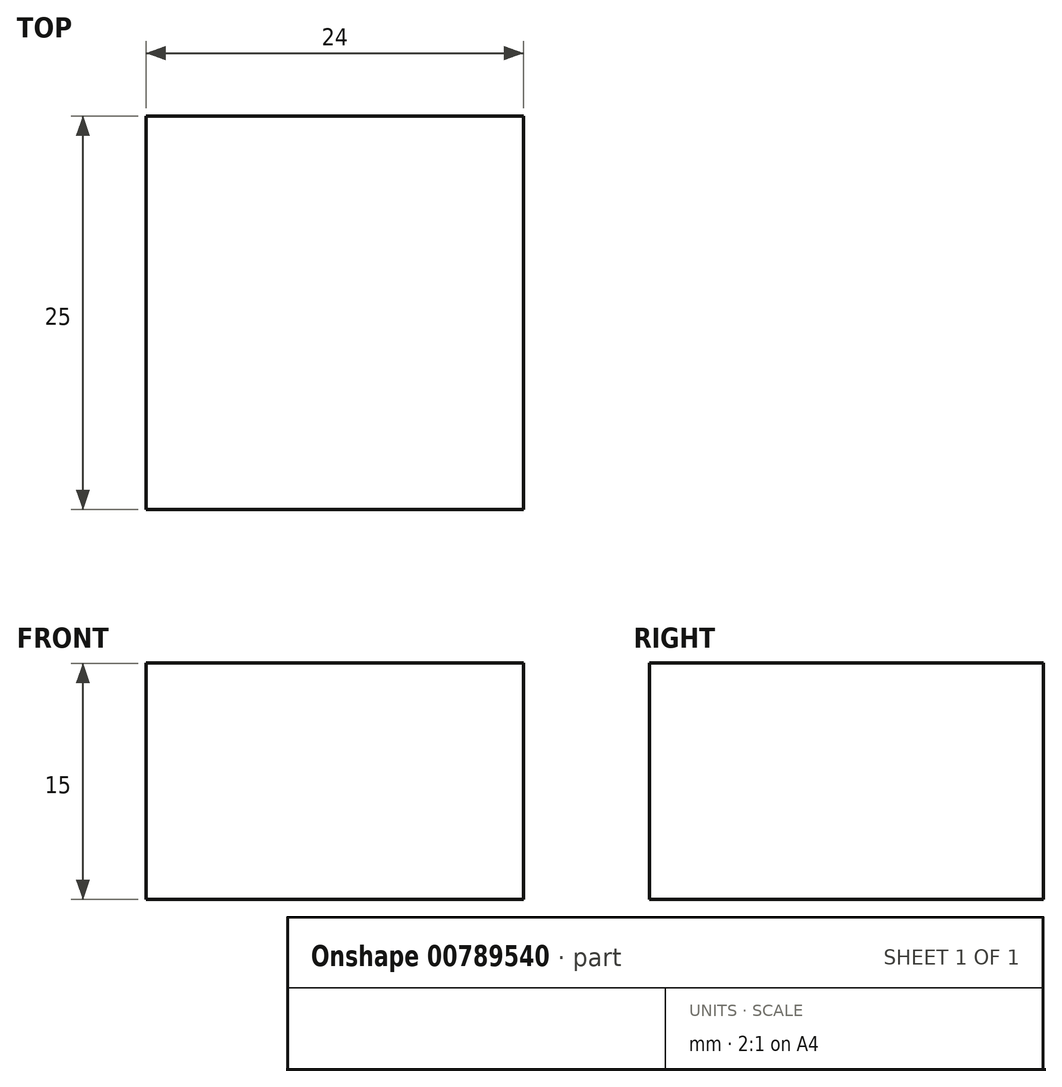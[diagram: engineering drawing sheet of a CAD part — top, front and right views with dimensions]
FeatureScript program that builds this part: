
annotation { "Feature Type Name" : "Feature", "Feature Type Description" : "" }
export const myFeature = defineFeature(function(context is Context, id is Id, definition is map)
    precondition{}
    {
        {
            var Q0;
            Q0=qCreatedBy(makeId("Front.planeOp"),FACE);
            var sketch = newSketch(context, id + "F0", { "sketchPlane" : qUnion([Q0])});
            skLineSegment(sketch, "E0.bottom", {"start": v(11.71, 2.54) * mm, "end": v(-13.29, 2.54) * mm});
            skLineSegment(sketch, "E0.top", {"start": v(11.71, -12.46) * mm, "end": v(-23.29, -12.46) * mm});
            skLineSegment(sketch, "E0.left", {"start": v(11.71, 2.54) * mm, "end": v(11.71, -12.46) * mm});
            skLineSegment(sketch, "E0.right", {"start": v(-12.29, 12.54) * mm, "end": v(-12.29, -12.46) * mm});
            skSolve(sketch);
        }
        {
            var Q0;
            Q0=qSketchRegion(id+"F0",true);
            extrude(context, id + "F1", {"entities" : qUnion([Q0]), "endBound" : BoundingType.SYMMETRIC, "depth" : 25 * mm, "offsetDistance" : 25 * mm});
        }
    });
